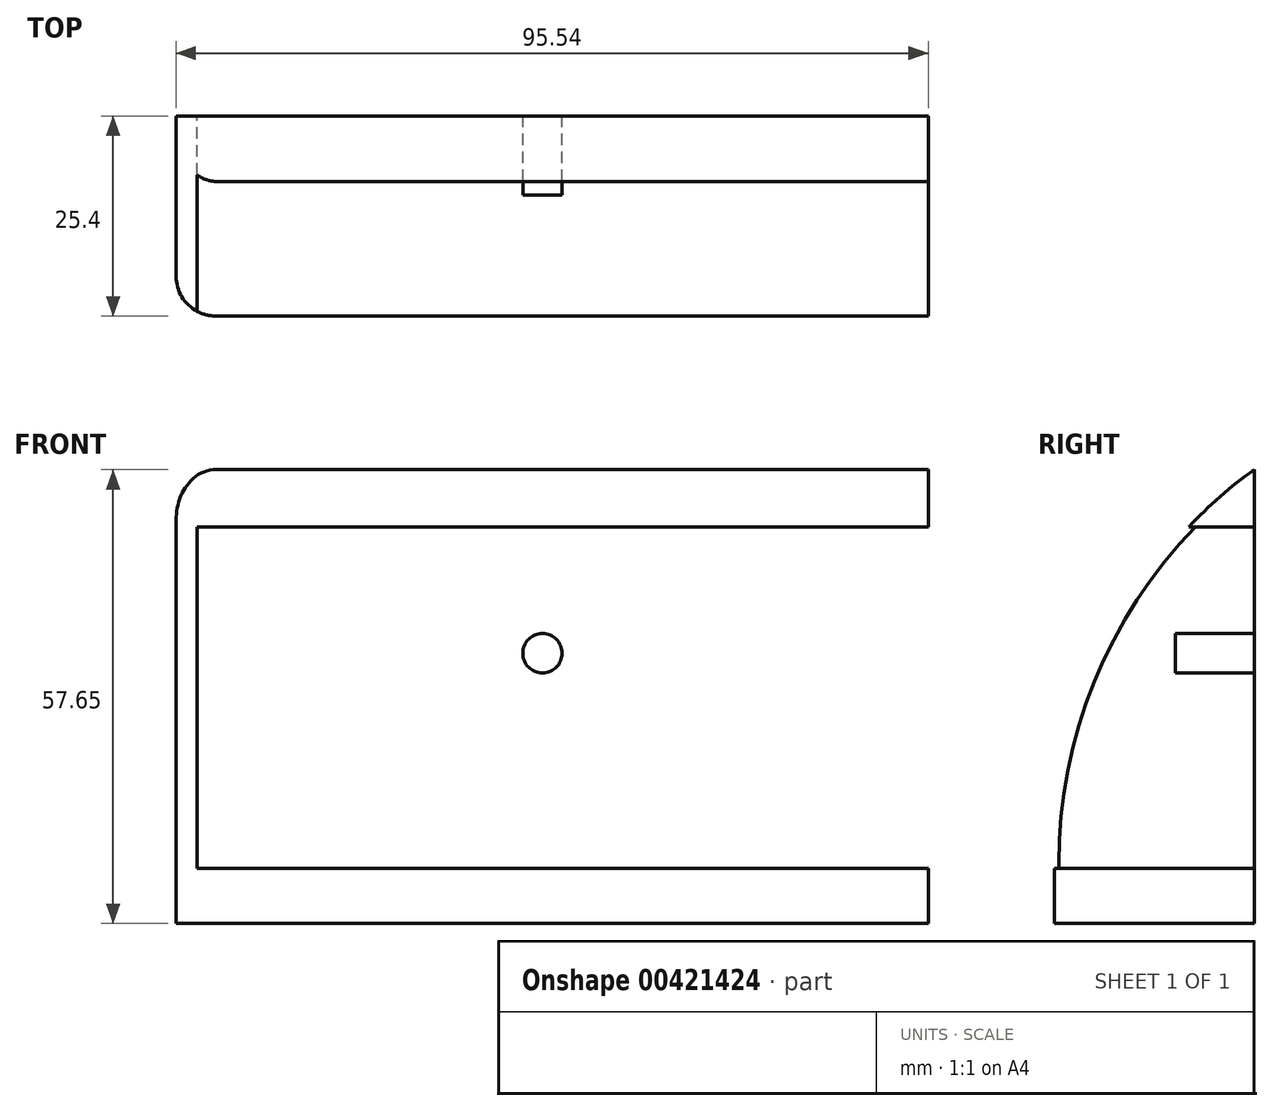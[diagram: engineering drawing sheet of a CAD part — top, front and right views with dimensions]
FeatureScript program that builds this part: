
annotation { "Feature Type Name" : "Feature", "Feature Type Description" : "" }
export const myFeature = defineFeature(function(context is Context, id is Id, definition is map)
    precondition{}
    {
        {
            var Q0;
            Q0=qCreatedBy(makeId("Front.planeOp"),FACE);
            var sketch = newSketch(context, id + "F0", { "sketchPlane" : qUnion([Q0])});
            skCircle(sketch, "E0", {"center": v(0, 0) * mm, "radius": 2.5 * mm});
            skSolve(sketch);
        }
        {
            var Q0;
            Q0=makeQuery(id+"F0.imprint","IMPRINT",FACE,{"disambiguationData":[TD([[makeQuery(id+"F0.imprint","IMPRINT",EDGE,{"derivedFrom":sQuery(id+"F0.wireOp",EDGE,"E0")}),1.0]])]});
            extrude(context, id + "F1", {"entities" : qUnion([Q0]), "depth" : 10 * mm});
        }
        {
            var Q0;
            Q0=qCreatedBy(makeId("Front.planeOp"),FACE);
            var sketch = newSketch(context, id + "F2", { "sketchPlane" : qUnion([Q0])});
            skLineSegment(sketch, "E1.bottom", {"start": v(-43.85, 16.06) * mm, "end": v(49, 16.06) * mm});
            skLineSegment(sketch, "E1.top", {"start": v(-43.85, -27.3) * mm, "end": v(49, -27.3) * mm});
            skLineSegment(sketch, "E1.left", {"start": v(-43.85, 16.06) * mm, "end": v(-43.85, -27.3) * mm});
            skLineSegment(sketch, "E1.right", {"start": v(49, 16.06) * mm, "end": v(49, -27.3) * mm});
            skLineSegment(sketch, "E2.bottom", {"start": v(49, 16.06) * mm, "end": v(49, 16.06) * mm});
            skLineSegment(sketch, "E2.top", {"start": v(49, 23.33) * mm, "end": v(49, 23.33) * mm});
            skLineSegment(sketch, "E2.left", {"start": v(49, 16.06) * mm, "end": v(49, 23.33) * mm});
            skLineSegment(sketch, "E2.right", {"start": v(49, 16.06) * mm, "end": v(49, 23.33) * mm});
            skLineSegment(sketch, "E3.bottom", {"start": v(49, 23.33) * mm, "end": v(-46.54, 23.33) * mm});
            skLineSegment(sketch, "E3.top", {"start": v(49, -34.32) * mm, "end": v(-46.54, -34.32) * mm});
            skLineSegment(sketch, "E3.left", {"start": v(49, 23.33) * mm, "end": v(49, -34.32) * mm});
            skLineSegment(sketch, "E3.right", {"start": v(-46.54, 23.33) * mm, "end": v(-46.54, -34.32) * mm});
            skSolve(sketch);
        }
        {
            var Q0;
            {var subQ2=sQuery(id+"F2.wireOp",EDGE,"E1.bottom");Q0=makeQuery(id+"F2.imprint","IMPRINT",FACE,{"disambiguationData":[TD([[makeQuery(id+"F2.imprint","IMPRINT",EDGE,{"derivedFrom":subQ2}),1.0]])]});}
            extrude(context, id + "F3", {"entities" : qUnion([Q0]), "depth" : 25.4 * mm});
        }
        {
            var Q0;
            Q0=makeQuery(id+"F3.opExtrude","CAP_EDGE",EDGE,{"disambiguationData":[OSD([sQuery(id+"F2.wireOp",EDGE,"E3.bottom")])],"isStart":false});
            fillet(context, id + "F4", {"entities" : qUnion([Q0]), "radius" : 61.93 * mm, "tangentPropagation" : true, "allowEdgeOverflow" : false});
        }
        {
            var Q0;
            Q0=makeQuery(id+"F4.opFillet","BLEND_EDGE",EDGE,{"blendedFrom":[makeQuery(id+"F3.opExtrude","CAP_EDGE",EDGE,{"disambiguationData":[OSD([sQuery(id+"F2.wireOp",EDGE,"E3.bottom")])],"isStart":false}),makeQuery(id+"F3.opExtrude","SWEPT_FACE",FACE,{"disambiguationData":[OSD([sQuery(id+"F2.wireOp",EDGE,"E3.right")])]})],"blendedInto":[makeQuery(id+"F3.opExtrude","SWEPT_FACE",FACE,{"disambiguationData":[OSD([sQuery(id+"F2.wireOp",EDGE,"E3.right")])]})]});
            fillet(context, id + "F5", {"entities" : qUnion([Q0]), "radius" : 5.08 * mm, "tangentPropagation" : true, "allowEdgeOverflow" : false});
        }
    });
